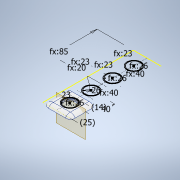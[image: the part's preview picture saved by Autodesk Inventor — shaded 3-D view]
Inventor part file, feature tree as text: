
AUTODESK INVENTOR PART (.ipt)
format: ipt  version: 2021 (Build 250183000, 183)  size: 2,222,080 bytes
history: native  units: in
note: dims shown in document units (in); Inventor stores cm internally (conversion verified against a paired STEP export)
features: extrude x11, other x9, fillet x3, sketch x2
ambient origin geometry x8: Origin, YZ Plane, XZ Plane, XY Plane, X Axis, Y Axis, Z Axis, Center Point
bodies: Body1 (feature_tree)
feature tree (25):
  extrude  "Base"  Depth=2.0472in
  other  "Top Indent Sketch"
  extrude  "Top"  Depth=1.0236in
  extrude  "Walls"  Depth=1.0236in
  fillet  "Outer"  Radius=1.0236in
  extrude  "Outer Wire"  Depth=1.0236in
  extrude  "Wall Holes"  Depth=1.5748in
  extrude  "Text"  Depth=1.5748in
  extrude  "Inner Sketch"  Depth=1.5748in
  fillet  "Inner Fillet"  Radius=0.7087in
  extrude  "halfer"  Depth=0.315in
  extrude  "Top Indent"  Depth=0.315in
  other  "Wire Hole Plane"
  extrude  "Wire Hole"  Depth=0.2362in
  fillet  "Fillet9"  Radius=0.2362in
  extrude  "Extrusion20"  Depth=1.4567in
  other  "Base Sketch"
  other  "Walls Sketch"
  other  "Outer Wire Sketch"
  other  "Wall Holes Sketch"
  other  "Text Sketch"
  other  "Inner Support Sketch"
  sketch  "Sketch25"  dims[d6=6.6929in d7=2.0472in]
  other  "Wire Hole Sketch"
  sketch  "Sketch28"  dims[d8=1.7717in d9=0.0in d10=1.0236in d11=1.0236in d12=1.0236in d13=1.0236in d14=1.5748in d15=1.5748in d16=1.5748in d19=0.7087in d20=0.0in d21=0.315in d22=0.315in d23=0.2362in d24=0.2362in d25=1.4567in d26=0.0in d27=0.9055in d28=0.9055in d29=0.9055in d30=0.9055in d31=0.7874in d32=3.3465in d33=1.5748in d35=0.9843in d36=0.3937in d38=0.3937in d39=0.0in d52=0.315in d55=0.1969in d56=0.0in d58=0.5512in d65=0.315in d66=0.1575in d67=0.1575in d68=0.315in d69=0.2774in d70=0.2774in d71=0.0499in d72=0.0499in d73=1.6535in d74=0.0in d77=0.6496in d81=0.9843in d82=0.0in d85=0.5906in d86=0.1575in d87=0.1575in d88=1.0236in d89=0.315in d90=0.1575in d92=0.0in d93=0.1181in d94=0.0in d95=0.1575in d96=0.6496in d143=0.0in d144=0.0in d155=4.9213in d156=0.0in d158=0.0945in d159=0.0in d162=0.2362in d163=0.0in d164=0.0in d165=0.1969in d166=0.2362in d167=0.0in d168=0.1969in d169=0.1969in d170=4.7244in d171=0.0in d172=3.3465in d173=1.0236in d174=0.0394in d175=1.2992in d176=1.5748in d177=0.0in d44=0.0197in d45=0.0344in d46=0.0197in d47=0.0344in d48=0.0197in d49=0.0344in d59=0.0197in d60=0.0344in d61=0.0197in d62=0.0344in d178=0.0344in]
